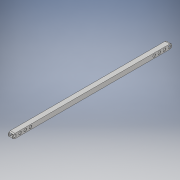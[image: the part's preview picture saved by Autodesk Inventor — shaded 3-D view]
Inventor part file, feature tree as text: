
AUTODESK INVENTOR PART (.ipt)
format: ipt  version: 2018 (Build 220112000, 112)  size: 154,624 bytes
history: native  units: in
note: dims shown in document units (in); Inventor stores cm internally (conversion verified against a paired STEP export)
features: extrude x3, sketch x3, fillet x1
ambient origin geometry x8: Origin, YZ Plane, XZ Plane, XY Plane, X Axis, Y Axis, Z Axis, Center Point
bodies: Solid1 (feature_tree)
feature tree (7):
  extrude  "Extrusion1"  Depth=1.0in
  fillet  "Fillet1"  Radius=34.0in
  extrude  "Extrusion2"  Depth=0.1in
  extrude  "Extrusion3"  Depth=0.1in
  sketch  "Sketch1"  dims[d0=1.0in d1=1.0in d2=34.0in d3=0.0in]
  sketch  "Sketch2"  dims[d4=0.5in d5=0.1in]
  sketch  "Sketch3"  dims[d6=0.1in d7=0.1in d8=0.1in d9=40.0in d10=0.0in d11=0.6175in d12=0.6175in d13=0.6175in d14=0.6175in d15=0.6175in d16=0.6175in d17=0.6175in d18=0.6175in d19=0.5in d20=0.5in d21=0.5in d22=0.5in d23=0.5in d24=0.5in d25=0.5in d26=0.5in d27=0.0in d28=1.1in d29=1.1in d30=1.1in d31=0.0in d32=1.1in d33=1.1in d34=1.1in d35=1.0in d36=0.0in]
